# Revit family: 50136 Varionaut 90
name_source: partatom
category: Körper
revit_build: Autodesk Revit 2015 (Build: 20140606_1530(x64)
units: mm (PartAtom-declared; Revit-internal decimal feet)

## types (1)
- Varionaut 90/24V/DMX/02
    Beschreibung = controllable pump
    Dimension incl. filter LxWxH = 268x142x170 mm
    Dynamic behaviour speed/ time to reach full fountain height from 0 - 100% with comet 5-8 = 0,6 s
    Environmental conditions, dry application = Ambient temperature max. 30°C with natural convection, max 40°C with forced convection no direct sun exposure permitted
    Environmental conditions, submersible application = Water temperature min. 4°C to max. 35°C
    Filter housing = Plastic / stainless steel 1.4301 (AISI 304)
    Filter surface = 200 cm²
    H max = 2.6 m
    Hersteller = OASE GmbH Post Box 2069, 48469 Hörstel , Germany +49 5454 80-0
    Homepage = http://www.oase-livingwater.com
    Immersion depth max. = 4 m
    Input DMX = 1 m BUS cable with DMX box
    Input power = 1 m power cable wit power box
    Max. powering up / min. Off time = 1 x per minute / 10 s
    Modell = Varionaut 90/24V/DMX/02
    MotorType / Electronic = 24 V DC EC-Motor, DMX controlled
    Name = controllable pump
    Norminal voltage = 24 V/DC
    Number of BMX chanels = 2 channels (control channel, speed channel)
    Pressure side connection = 1 inch
    Protection class = IP 68
    Pump housing = Plastic
    Q max = 95 l/min
    Qmin Offset-Modus - DMX 0 = 26 l/min
    Suction side connection = 1 1/2 inch
    Weight = 3.70 kg
    oder no. = 50136
    power max. = 60.00 W

## geometry (parser evidence)
native form markers: Blend x6
no freeform markers — native parametric forms only
